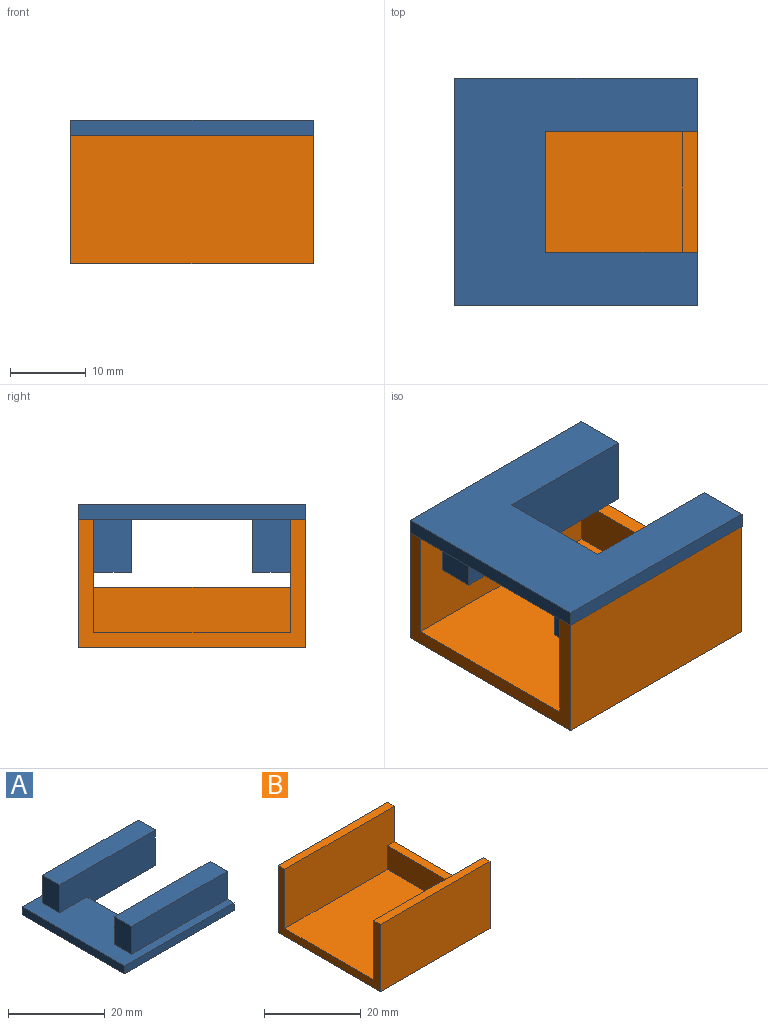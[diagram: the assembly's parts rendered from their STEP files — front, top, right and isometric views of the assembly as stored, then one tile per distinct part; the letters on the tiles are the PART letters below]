
ASSEMBLY  parts=2 mates=1
PART A: 16 faces, bbox 32x30x9 mm
  f0: plane 32x30mm, normal (0,0,1), area 360mm2, adj f1,f2,f3,f4,f5,f7,f8,f9
  f1: plane 9x7mm, normal (1,0,0), area 49mm2, adj f0,f5,f6,f9,f14,f15
  f2: plane 9x7mm, normal (1,0,0), area 49mm2, adj f0,f3,f6,f7,f10,f12
  f3: plane 32x2mm, normal (0,1,0), area 64mm2, adj f0,f2,f4,f6
  f4: plane 30x2mm, normal (-1,0,0), area 60mm2, adj f0,f3,f5,f6
  f5: plane 32x2mm, normal (0,-1,0), area 64mm2, adj f0,f1,f4,f6
  f6: plane 32x30mm, normal (0,0,-1), area 640mm2, adj f1,f2,f3,f4,f5,f7,f8,f9
  f7: plane 28x9mm, normal (0,-1,0), area 236mm2, adj f0,f2,f6,f8,f11,f12
  f8: plane 16x2mm, normal (1,0,0), area 32mm2, adj f0,f6,f7,f9
  f9: plane 28x9mm, normal (0,1,0), area 236mm2, adj f0,f1,f6,f8,f13,f15
  f10: plane 28x7mm, normal (0,1,0), area 196mm2, adj f0,f2,f11,f12
  f11: plane 7x5mm, normal (-1,0,0), area 35mm2, adj f0,f7,f10,f12
  f12: plane 28x5mm, normal (0,0,1), area 140mm2, adj f2,f7,f10,f11
  f13: plane 7x5mm, normal (-1,0,0), area 35mm2, adj f0,f9,f14,f15
  f14: plane 28x7mm, normal (0,-1,0), area 196mm2, adj f0,f1,f13,f15
  f15: plane 28x5mm, normal (0,0,1), area 140mm2, adj f1,f9,f13,f14
PART B: 12 faces, bbox 32x30x17 mm
  f0: plane 26x6mm, normal (-1,0,0), area 156mm2, adj f1,f2,f8,f10
  f1: plane 26x2mm, normal (0,0,1), area 52mm2, adj f0,f3,f8,f10
  f2: plane 30x26mm, normal (0,0,1), area 780mm2, adj f0,f5,f8,f10
  f3: plane 30x17mm, normal (1,0,0), area 276mm2, adj f1,f4,f6,f7,f8,f9,f10,f11
  f4: plane 32x17mm, normal (0,1,0), area 544mm2, adj f3,f5,f7,f11
  f5: plane 30x17mm, normal (-1,0,0), area 120mm2, adj f2,f4,f6,f7,f8,f9,f10,f11
  f6: plane 32x17mm, normal (0,-1,0), area 544mm2, adj f3,f5,f7,f9
  f7: plane 32x30mm, normal (0,0,-1), area 960mm2, adj f3,f4,f5,f6
  f8: plane 32x15mm, normal (0,1,0), area 468mm2, adj f0,f1,f2,f3,f5,f9
  f9: plane 32x2mm, normal (0,0,1), area 64mm2, adj f3,f5,f6,f8
  f10: plane 32x15mm, normal (0,-1,0), area 468mm2, adj f0,f1,f2,f3,f5,f11
  f11: plane 32x2mm, normal (0,0,1), area 64mm2, adj f3,f4,f5,f10
PLACE A rot(axis=(1,0,0),180deg) t=(-105.01,-33.41,20.77)mm
PLACE B t=(-16.53,-2.7,1.77)mm
MATE fastened A.f0 <-> B.f11  axis (0,0,-1) through (-0.53,10.3,18.77)mm
